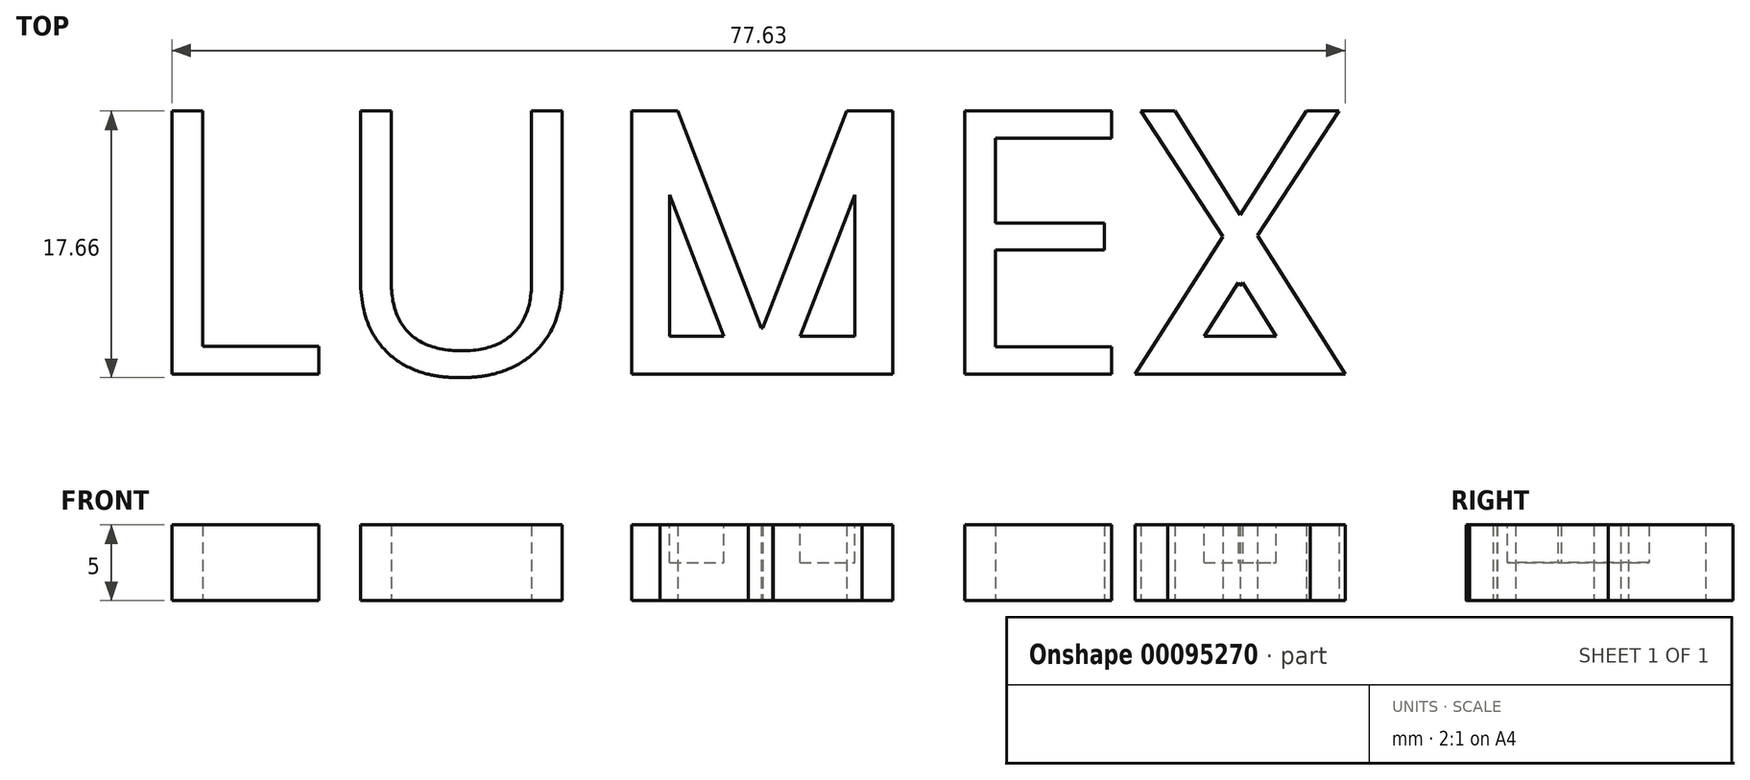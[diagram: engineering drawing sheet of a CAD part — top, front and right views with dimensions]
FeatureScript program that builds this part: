
annotation { "Feature Type Name" : "Feature", "Feature Type Description" : "" }
export const myFeature = defineFeature(function(context is Context, id is Id, definition is map)
    precondition{}
    {
        {
            var Q0;
            Q0=qCreatedBy(makeId("Top.planeOp"),FACE);
            var sketch = newSketch(context, id + "F0", { "sketchPlane" : qUnion([Q0])});
            skText(sketch, "E0", { "text": "LUMEX", "fontName": "OpenSans-Regular.ttf"});
            skLineSegment(sketch, "E1", {"start": v(-8.74, -17.57) * mm, "end": v(71.26, -17.57) * mm});
            const initialGuessF0  = {"E0": [-0.00874, -0.01757, 1, 0, 0.01757]};
            skSetInitialGuess(sketch, initialGuessF0);
            skSolve(sketch);
        }
        {
            var Q0;
            Q0 = qSketchRegion(id + "F0", true);
            extrude(context, id + "F1", {"entities" : qUnion([Q0]), "depth" : 5 * mm});
        }
        {
            var Q0;
            Q0=sQuery(id+"F0.wireOp",EDGE,"E1");
            extrude(context, id + "F2", {"bodyType" : ToolBodyType.SURFACE, "surfaceEntities" : qUnion([Q0]), "depth" : 3 * mm});
        }
        {
            var Q0;
            Q0=makeQuery(id+"F1.opExtrude","CAP_FACE",FACE,{"disambiguationData":[OSD([sQuery(id+"F0.wireOp",EDGE,"E0.sketch_text.stroke-25"),sQuery(id+"F0.wireOp",EDGE,"E0.sketch_text.stroke-26"),sQuery(id+"F0.wireOp",EDGE,"E0.sketch_text.stroke-27"),sQuery(id+"F0.wireOp",EDGE,"E0.sketch_text.stroke-28"),sQuery(id+"F0.wireOp",EDGE,"E0.sketch_text.stroke-29"),sQuery(id+"F0.wireOp",EDGE,"E0.sketch_text.stroke-30"),sQuery(id+"F0.wireOp",EDGE,"E0.sketch_text.stroke-31"),sQuery(id+"F0.wireOp",EDGE,"E1")])],"isStart":false});
            shell(context, id + "F3", {"entities" : qUnion([Q0]), "thickness" : 2.5 * mm});
        }
        {
            var Q0;
            Q0=makeQuery(id+"F1.opExtrude","CAP_FACE",FACE,{"disambiguationData":[OSD([sQuery(id+"F0.wireOp",EDGE,"E0.sketch_text.stroke-54"),sQuery(id+"F0.wireOp",EDGE,"E0.sketch_text.stroke-55"),sQuery(id+"F0.wireOp",EDGE,"E0.sketch_text.stroke-56"),sQuery(id+"F0.wireOp",EDGE,"E0.sketch_text.stroke-57"),sQuery(id+"F0.wireOp",EDGE,"E0.sketch_text.stroke-58"),sQuery(id+"F0.wireOp",EDGE,"E0.sketch_text.stroke-59"),sQuery(id+"F0.wireOp",EDGE,"E0.sketch_text.stroke-60"),sQuery(id+"F0.wireOp",EDGE,"E0.sketch_text.stroke-61"),sQuery(id+"F0.wireOp",EDGE,"E1")])],"isStart":false});
            shell(context, id + "F4", {"entities" : qUnion([Q0]), "thickness" : 2.5 * mm});
        }
    });
